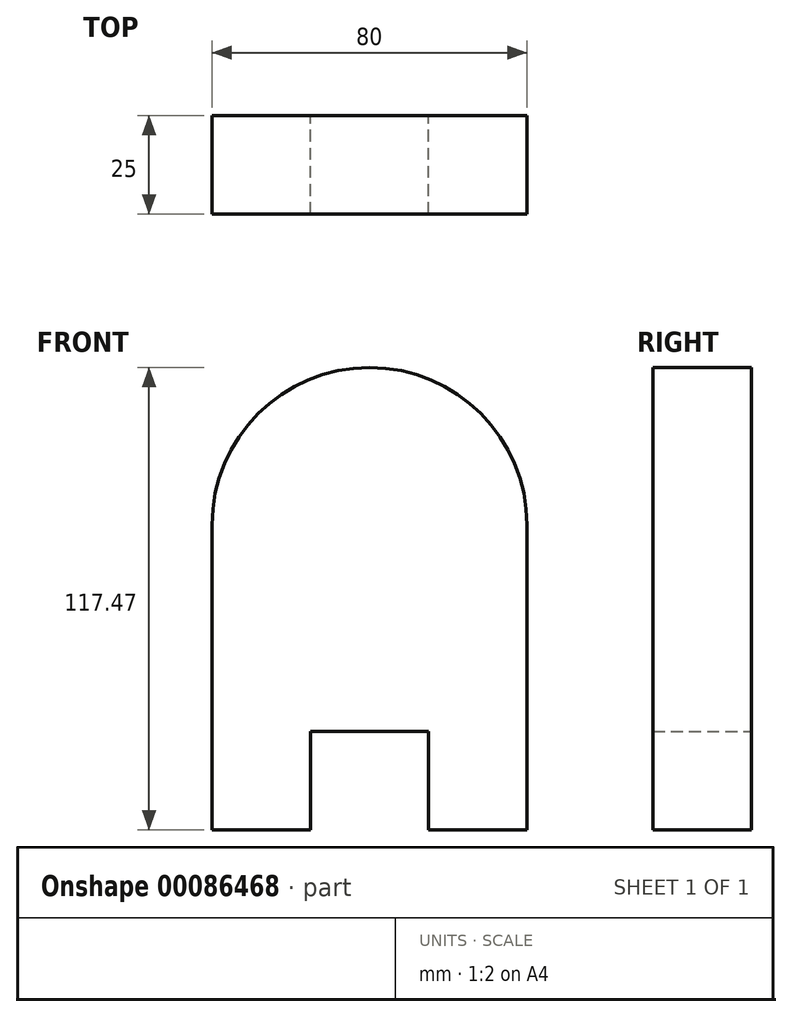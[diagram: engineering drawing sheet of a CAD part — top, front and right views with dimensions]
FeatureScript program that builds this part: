
annotation { "Feature Type Name" : "Feature", "Feature Type Description" : "" }
export const myFeature = defineFeature(function(context is Context, id is Id, definition is map)
    precondition{}
    {
        {
            var Q0;
            Q0=qCreatedBy(makeId("Front.planeOp"),FACE);
            var sketch = newSketch(context, id + "F0", { "sketchPlane" : qUnion([Q0])});
            skCircle(sketch, "E0", {"center": v(0, 0) * mm, "radius": 40 * mm});
            skLineSegment(sketch, "E1", {"start": v(40, 0) * mm, "end": v(40, -77.47) * mm});
            skLineSegment(sketch, "E2", {"start": v(40, -77.47) * mm, "end": v(15, -77.47) * mm});
            skLineSegment(sketch, "E3", {"start": v(15, -77.47) * mm, "end": v(15, -52.47) * mm});
            skLineSegment(sketch, "E4", {"start": v(15, -52.47) * mm, "end": v(-15, -52.47) * mm});
            skLineSegment(sketch, "E5", {"start": v(-15, -52.47) * mm, "end": v(-15, -77.47) * mm});
            skLineSegment(sketch, "E6", {"start": v(-15, -77.47) * mm, "end": v(-40, -77.47) * mm});
            skLineSegment(sketch, "E7", {"start": v(-40, -77.47) * mm, "end": v(-40, 0) * mm});
            skSolve(sketch);
        }
        {
            var Q0;
            Q0 = qSketchRegion(id + "F0", true);
            extrude(context, id + "F1", {"entities" : qUnion([Q0]), "depth" : 25 * mm});
        }
    });
